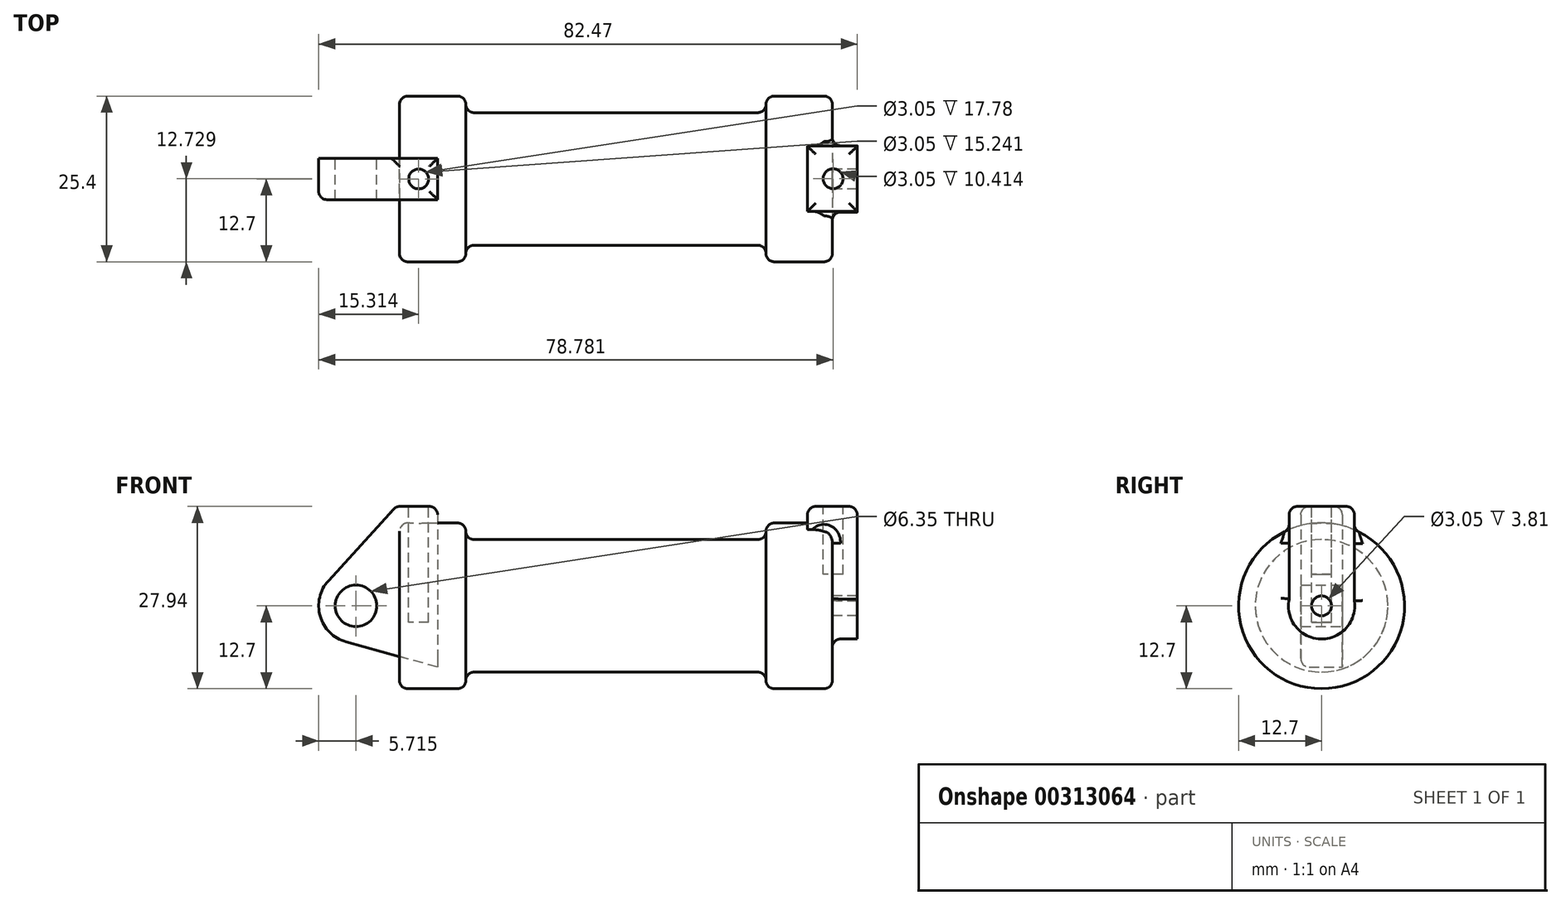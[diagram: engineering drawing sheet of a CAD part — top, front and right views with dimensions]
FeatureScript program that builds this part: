
annotation { "Feature Type Name" : "Feature", "Feature Type Description" : "" }
export const myFeature = defineFeature(function(context is Context, id is Id, definition is map)
    precondition{}
    {
        {
            var Q0;
            Q0=qCreatedBy(makeId("Front.planeOp"),FACE);
            var sketch = newSketch(context, id + "F0", { "sketchPlane" : qUnion([Q0])});
            skLineSegment(sketch, "E0", {"start": v(0, 0) * mm, "end": v(0, 12.7) * mm});
            skLineSegment(sketch, "E1", {"start": v(0, 12.7) * mm, "end": v(10.16, 12.7) * mm});
            skLineSegment(sketch, "E2", {"start": v(10.16, 12.7) * mm, "end": v(10.16, 10.16) * mm});
            skLineSegment(sketch, "E3", {"start": v(10.16, 10.16) * mm, "end": v(56.13, 10.16) * mm});
            skLineSegment(sketch, "E4", {"start": v(56.13, 10.16) * mm, "end": v(56.13, 12.7) * mm});
            skLineSegment(sketch, "E5", {"start": v(56.13, 12.7) * mm, "end": v(66.3, 12.7) * mm});
            skLineSegment(sketch, "E6", {"start": v(66.3, 12.7) * mm, "end": v(66.3, 0) * mm});
            skLineSegment(sketch, "E7", {"start": v(66.3, 0) * mm, "end": v(0, 0) * mm});
            skLineSegment(sketch, "E8", {"start": v(5.84, 15.24) * mm, "end": v(-0.5, 15.24) * mm});
            skLineSegment(sketch, "E9", {"start": v(-0.5, 15.24) * mm, "end": v(-10.88, 3.85) * mm});
            skLineSegment(sketch, "E10", {"start": v(0, 0) * mm, "end": v(-6.65, 0) * mm});
            skCircle(sketch, "E11", {"center": v(-6.65, 0) * mm, "radius": 5.72 * mm});
            skCircle(sketch, "E12", {"center": v(-6.65, 0) * mm, "radius": 3.18 * mm});
            skLineSegment(sketch, "E13", {"start": v(5.84, 15.24) * mm, "end": v(5.84, -9.4) * mm});
            skLineSegment(sketch, "E14", {"start": v(5.84, -9.4) * mm, "end": v(-8.18, -5.5) * mm});
            skSolve(sketch);
        }
        {
            var Q0;
            {var subQ0=sQuery(id+"F0.wireOp",EDGE,"E2");Q0=makeQuery(id+"F0.imprint","IMPRINT",FACE,{"disambiguationData":[TD([[makeQuery(id+"F0.imprint","IMPRINT",EDGE,{"derivedFrom":subQ0}),-1.0]])]});}
            var Q1;
            {var subQ0=sQuery(id+"F0.wireOp",EDGE,"E0");Q1=makeQuery(id+"F0.imprint","IMPRINT",FACE,{"disambiguationData":[TD([[makeQuery(id+"F0.imprint","IMPRINT",EDGE,{"derivedFrom":subQ0}),-1.0]])]});}
            var Q2;
            Q2=sQuery(id+"F0.wireOp",EDGE,"E7");
            revolve(context, id + "F1", {"entities" : qUnion([Q0, Q1]), "axis" : qUnion([Q2]), "revolveType" : RevolveType.FULL});
        }
        {
            var Q0;
            {var subQ1=sQuery(id+"F0.wireOp",EDGE,"E0");Q0=makeQuery(id+"F0.imprint","IMPRINT",FACE,{"disambiguationData":[TD([[makeQuery(id+"F0.imprint","IMPRINT",EDGE,{"derivedFrom":subQ1}),1.0]])]});}
            var Q1;
            {var subQ0=sQuery(id+"F0.wireOp",EDGE,"E0");Q1=makeQuery(id+"F0.imprint","IMPRINT",FACE,{"disambiguationData":[TD([[makeQuery(id+"F0.imprint","IMPRINT",EDGE,{"derivedFrom":subQ0}),-1.0]])]});}
            var Q2;
            {var subQ0=sQuery(id+"F0.wireOp",EDGE,"E14");Q2=makeQuery(id+"F0.imprint","IMPRINT",FACE,{"disambiguationData":[TD([[makeQuery(id+"F0.imprint","IMPRINT",EDGE,{"derivedFrom":subQ0}),-1.0]])]});}
            var Q3;
            {var subQ5=sQuery(id+"F0.wireOp",EDGE,"E12");Q3=makeQuery(id+"F0.imprint","IMPRINT",FACE,{"disambiguationData":[TD([[makeQuery(id+"F0.imprint","IMPRINT",EDGE,{"derivedFrom":subQ5}),-1.0]])]});}
            extrude(context, id + "F2", {"entities" : qUnion([Q0, Q1, Q2, Q3]), "endBound" : BoundingType.SYMMETRIC, "depth" : 6.35 * mm});
        }
        {
            var Q0;
            Q0=makeQuery(id+"F1.opRevolve","SWEPT_FACE",FACE,{"disambiguationData":[OSD([sQuery(id+"F0.wireOp",EDGE,"E6")])]});
            var sketch = newSketch(context, id + "F3", { "sketchPlane" : qUnion([Q0])});
            skCircle(sketch, "E15", {"center": v(0, 0) * mm, "radius": 1.52 * mm});
            skCircle(sketch, "E16", {"center": v(0, 0) * mm, "radius": 5.08 * mm});
            skSolve(sketch);
        }
        {
            var Q0;
            Q0=makeQuery(id+"F3.imprint","IMPRINT",FACE,{"disambiguationData":[TD([[makeQuery(id+"F3.imprint","IMPRINT",EDGE,{"derivedFrom":sQuery(id+"F3.wireOp",EDGE,"E15")}),-1.0]])]});
            var sketch = newSketch(context, id + "F4", { "sketchPlane" : qUnion([Q0])});
            skLineSegment(sketch, "E17", {"start": v(-4.97, 0) * mm, "end": v(-4.97, 15.24) * mm});
            skLineSegment(sketch, "E18", {"start": v(5.03, 0) * mm, "end": v(5.03, 15.24) * mm});
            skLineSegment(sketch, "E19", {"start": v(-4.97, 15.24) * mm, "end": v(5.03, 15.24) * mm});
            skSolve(sketch);
        }
        {
            var Q0;
            Q0=makeQuery(id+"F3.imprint","IMPRINT",FACE,{"disambiguationData":[TD([[makeQuery(id+"F3.imprint","IMPRINT",EDGE,{"derivedFrom":sQuery(id+"F3.wireOp",EDGE,"E15")}),-1.0]])]});
            var Q1;
            {var subQ0=sQuery(id+"F4.wireOp",EDGE,"E19");Q1=makeQuery(id+"F4.imprint","IMPRINT",FACE,{"disambiguationData":[TD([[makeQuery(id+"F4.imprint","IMPRINT",EDGE,{"derivedFrom":subQ0}),-1.0]])]});}
            extrude(context, id + "F5", {"entities" : qUnion([Q0, Q1]), "operationType" : NewBodyOperationType.ADD, "endBound" : BoundingType.SYMMETRIC, "depth" : 7.62 * mm});
        }
        {
            var Q0;
            Q0=makeQuery(id+"F2.opExtrude","SWEPT_FACE",FACE,{"disambiguationData":[OSD([sQuery(id+"F0.wireOp",EDGE,"E8")])]});
            var sketch = newSketch(context, id + "F6", { "sketchPlane" : qUnion([Q0])});
            skCircle(sketch, "E20", {"center": v(2.94, 0) * mm, "radius": 1.52 * mm});
            skPoint(sketch, "E20.centerSnap0", {"position": v(-0.5, 0) * mm});
            skSolve(sketch);
        }
        {
            var Q0;
            Q0=makeQuery(id+"F5.opExtrude","SWEPT_FACE",FACE,{"disambiguationData":[OSD([sQuery(id+"F4.wireOp",EDGE,"E19")])]});
            var sketch = newSketch(context, id + "F7", { "sketchPlane" : qUnion([Q0])});
            skCircle(sketch, "E21", {"center": v(66.41, 0.03) * mm, "radius": 1.52 * mm});
            skPoint(sketch, "E21.centerSnap0", {"position": v(70.1, 0.03) * mm});
            skSolve(sketch);
        }
        {
            var Q0;
            Q0=makeQuery(id+"F6.imprint","IMPRINT",FACE,{"disambiguationData":[TD([[makeQuery(id+"F6.imprint","IMPRINT",EDGE,{"derivedFrom":sQuery(id+"F6.wireOp",EDGE,"E20")}),1.0]])]});
            var sketch = newSketch(context, id + "F8", { "sketchPlane" : qUnion([Q0])});
            skSolve(sketch);
        }
        {
            var Q0;
            Q0=makeQuery(id+"F8.imprint","IMPRINT",FACE,{"disambiguationData":[TD([[makeQuery(id+"F8.imprint","IMPRINT",EDGE,{"derivedFrom":makeQuery(id+"F6.imprint","IMPRINT",EDGE,{"derivedFrom":sQuery(id+"F6.wireOp",EDGE,"E20")})}),1.0]])]});
            extrude(context, id + "F9", {"entities" : qUnion([Q0]), "operationType" : NewBodyOperationType.REMOVE, "oppositeDirection" : true, "depth" : 17.78 * mm});
        }
        {
            var Q0;
            Q0=makeQuery(id+"F7.imprint","IMPRINT",FACE,{"disambiguationData":[TD([[makeQuery(id+"F7.imprint","IMPRINT",EDGE,{"derivedFrom":sQuery(id+"F7.wireOp",EDGE,"E21")}),1.0]])]});
            extrude(context, id + "F10", {"entities" : qUnion([Q0]), "operationType" : NewBodyOperationType.REMOVE, "oppositeDirection" : true, "depth" : 10.4 * mm});
        }
        {
            var Q0;
            Q0=makeQuery(id+"F1.opRevolve","SWEPT_FACE",FACE,{"disambiguationData":[OSD([sQuery(id+"F0.wireOp",EDGE,"E3")])]});
            fillet(context, id + "F11", {"entities" : qUnion([Q0]), "radius" : 1.27 * mm, "tangentPropagation" : true, "allowEdgeOverflow" : false});
        }
        {
            var Q0;
            Q0=makeQuery(id+"F5.boolean.opBoolean","SPLIT",FACE,{"disambiguationData":[TD([makeQuery(id+"F1.opRevolve","SWEPT_FACE",FACE,{"disambiguationData":[OSD([sQuery(id+"F0.wireOp",EDGE,"E5")])]})])],"derivedFrom":makeQuery(id+"F1.opRevolve","SWEPT_FACE",FACE,{"disambiguationData":[OSD([sQuery(id+"F0.wireOp",EDGE,"E6")])]})});
            fillet(context, id + "F12", {"entities" : qUnion([Q0]), "radius" : 1.27 * mm, "tangentPropagation" : true, "allowEdgeOverflow" : false});
        }
        {
            var Q0;
            Q0=makeQuery(id+"F1.opRevolve","SWEPT_FACE",FACE,{"disambiguationData":[OSD([sQuery(id+"F0.wireOp",EDGE,"E0")])]});
            fillet(context, id + "F13", {"entities" : qUnion([Q0]), "radius" : 1.27 * mm, "tangentPropagation" : true, "allowEdgeOverflow" : false});
        }
        {
            var Q0;
            Q0=makeQuery(id+"F2.opExtrude","CAP_EDGE",EDGE,{"disambiguationData":[OSD([sQuery(id+"F0.wireOp",EDGE,"E8")])],"isStart":true});
            var Q1;
            Q1=makeQuery(id+"F2.opExtrude","SWEPT_EDGE",EDGE,{"disambiguationData":[OSD([sQuery(id+"F0.wireOp",EDGE,"E8"),sQuery(id+"F0.wireOp",EDGE,"E13")])]});
            var Q2;
            Q2=makeQuery(id+"F2.opExtrude","CAP_EDGE",EDGE,{"disambiguationData":[OSD([sQuery(id+"F0.wireOp",EDGE,"E8")])],"isStart":false});
            var Q3;
            Q3=makeQuery(id+"F2.opExtrude","SWEPT_EDGE",EDGE,{"disambiguationData":[OSD([sQuery(id+"F0.wireOp",EDGE,"E8"),sQuery(id+"F0.wireOp",EDGE,"E9")])]});
            var Q4;
            Q4=makeQuery(id+"F2.opExtrude","CAP_EDGE",EDGE,{"disambiguationData":[OSD([sQuery(id+"F0.wireOp",EDGE,"E9")])],"isStart":false});
            var Q5;
            Q5=makeQuery(id+"F5.opExtrude","SWEPT_EDGE",EDGE,{"disambiguationData":[OSD([sQuery(id+"F4.wireOp",EDGE,"E17"),sQuery(id+"F4.wireOp",EDGE,"E19")])]});
            var Q6;
            Q6=makeQuery(id+"F5.opExtrude","CAP_EDGE",EDGE,{"disambiguationData":[OSD([sQuery(id+"F4.wireOp",EDGE,"E19")])],"isStart":true});
            var Q7;
            Q7=makeQuery(id+"F5.opExtrude","SWEPT_EDGE",EDGE,{"disambiguationData":[OSD([sQuery(id+"F4.wireOp",EDGE,"E18"),sQuery(id+"F4.wireOp",EDGE,"E19")])]});
            var Q8;
            Q8=makeQuery(id+"F5.opExtrude","CAP_EDGE",EDGE,{"disambiguationData":[OSD([sQuery(id+"F4.wireOp",EDGE,"E19")])],"isStart":false});
            var Q9;
            Q9=makeQuery(id+"F1.opRevolve","SWEPT_EDGE",EDGE,{"disambiguationData":[OSD([sQuery(id+"F0.wireOp",EDGE,"E1"),sQuery(id+"F0.wireOp",EDGE,"E2")])]});
            var Q10;
            Q10=makeQuery(id+"F1.opRevolve","SWEPT_EDGE",EDGE,{"disambiguationData":[OSD([sQuery(id+"F0.wireOp",EDGE,"E4"),sQuery(id+"F0.wireOp",EDGE,"E5")])]});
            fillet(context, id + "F14", {"entities" : qUnion([Q0, Q1, Q2, Q3, Q4, Q5, Q6, Q7, Q8, Q9, Q10]), "radius" : 1.27 * mm, "tangentPropagation" : true, "allowEdgeOverflow" : false});
        }
    });
